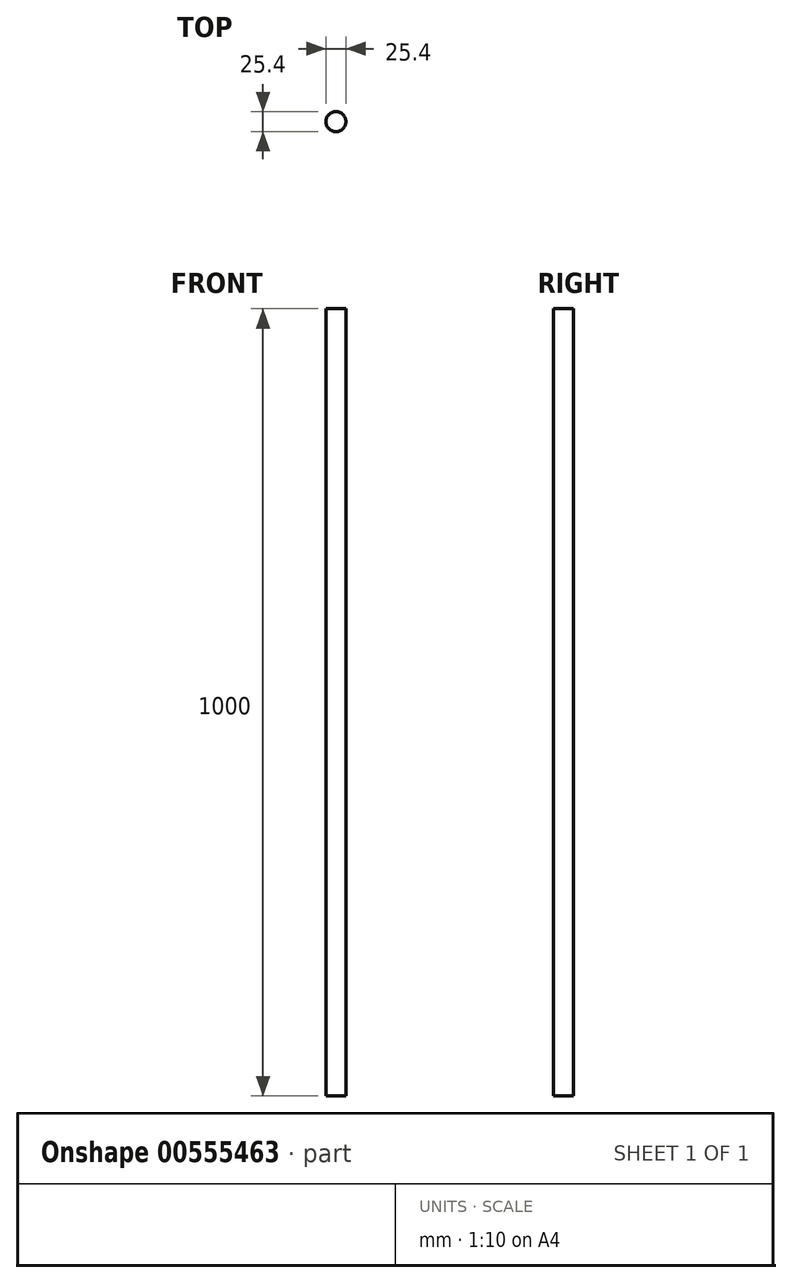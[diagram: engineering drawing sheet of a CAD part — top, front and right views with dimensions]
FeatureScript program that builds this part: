
annotation { "Feature Type Name" : "Feature", "Feature Type Description" : "" }
export const myFeature = defineFeature(function(context is Context, id is Id, definition is map)
    precondition{}
    {
        {
            var Q0;
            Q0=qCreatedBy(makeId("Top.planeOp"),FACE);
            var sketch = newSketch(context, id + "F0", { "sketchPlane" : qUnion([Q0])});
            skCircle(sketch, "E0", {"center": v(0, -3.81) * mm, "radius": 12.7 * mm});
            skSolve(sketch);
        }
        {
            var Q0;
            Q0=makeQuery(id+"F0.imprint","IMPRINT",FACE,{"disambiguationData":[TD([[makeQuery(id+"F0.imprint","IMPRINT",EDGE,{"derivedFrom":sQuery(id+"F0.wireOp",EDGE,"E0")}),1.0]])]});
            extrude(context, id + "F1", {"entities" : qUnion([Q0]), "depth" : 1000 * mm, "offsetDistance" : 25.4 * mm});
        }
    });
